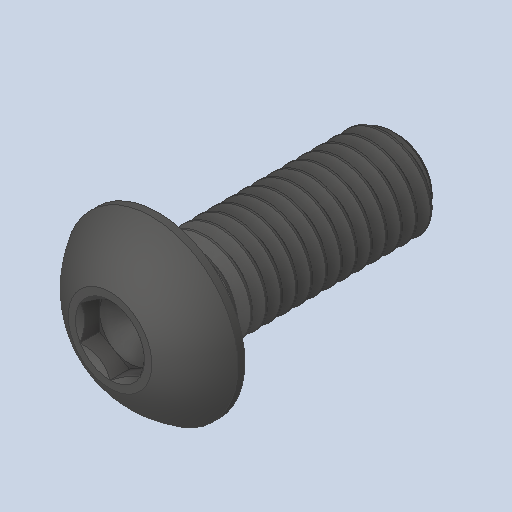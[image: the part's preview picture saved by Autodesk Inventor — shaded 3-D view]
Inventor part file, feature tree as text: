
AUTODESK INVENTOR PART (.ipt)
format: ipt  version: 2023 (Build 270158000, 158)  size: 545,792 bytes
history: native  units: in
note: dims shown in document units (in); Inventor stores cm internally (conversion verified against a paired STEP export)
features: revolve x1
ambient origin geometry x8: Origin, YZ Plane, XZ Plane, XY Plane, X Axis, Y Axis, Z Axis, Center Point
bodies: Solid1 (feature_tree)
feature tree (1):
  revolve  "Revolve2"  [1 undecoded]
note: 1 required parameter value undecoded (feature->parameter linkage not recoverable at this tier; creation-order binding heuristic only, values carry confidence <= 0.55)
